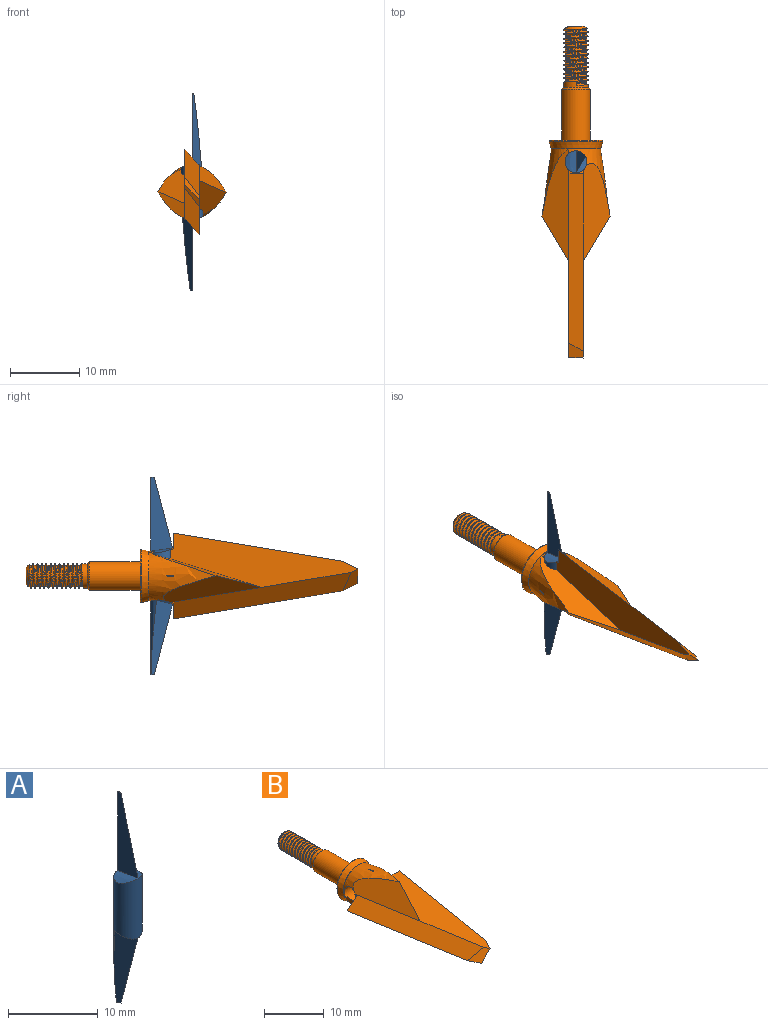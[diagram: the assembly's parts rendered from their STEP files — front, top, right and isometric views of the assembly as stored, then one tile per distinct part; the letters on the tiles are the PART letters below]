
ASSEMBLY  parts=2 mates=1
PART A: 11 faces, bbox 3.4x3.2x28.6 mm
  f0: cylinder r=1.59mm len=28.58mm, axis (0,0,-1), area 93.6mm2, adj f1,f2,f3,f4,f5,f6,f7,f8
  f1: plane 0.51x0.27mm, normal (0,0,-1), area 0.1mm2, adj f0,f3,f9
  f2: plane 0.51x0.27mm, normal (0,0,1), area 0.1mm2, adj f0,f4,f7
  f3: plane 10.69x3.18mm, normal (1,0,0), area 19.6mm2, adj f0,f1,f6,f9
  f4: plane 10.69x3.18mm, normal (-1,0,0), area 19.6mm2, adj f0,f2,f5,f7
  f5: cone r=3.56mm half-angle=8deg, axis (0,-1,0), area 4.1mm2, adj f0,f4
  f6: cone r=3.56mm half-angle=8deg, axis (0,-1,0), area 4.1mm2, adj f0,f3
  f7: plane 10.85x3.15mm, normal (0.87,-0.48,0.13), area 18.9mm2, adj f0,f2,f4,f8
  f8: cone r=3.56mm half-angle=8deg, axis (0,-1,0), area 1.6mm2, adj f0,f7
  f9: plane 10.85x3.15mm, normal (-0.87,-0.48,-0.13), area 18.9mm2, adj f0,f1,f3,f10
  f10: cone r=3.56mm half-angle=8deg, axis (0,-1,0), area 1.6mm2, adj f0,f9
PART B: 55 faces, bbox 12.4x285.9x9.8 mm
  f0: cylinder r=2.08mm len=7.37mm, axis (0,-1,0), area 96.4mm2, adj f2,f20
  f1: plane 3.66x3.66mm, normal (0,1,0), area 0.9mm2, adj f2,f36
  f2: cone r=1.83mm half-angle=45deg, axis (0,-1,0), area 4.4mm2, adj f0,f1
  f3: plane 0.63x0.29mm, normal (0,0,-1), area 0.1mm2, adj f6,f7,f30
  f4: cone r=3.56mm half-angle=8deg, axis (0,-1,0), area 37.2mm2, adj f5,f7,f18,f27,f28,f29,f30,f31
  f5: plane 0.63x0.29mm, normal (0,0,1), area 0.1mm2, adj f4,f7,f25
  f6: cone r=3.56mm half-angle=8deg, axis (0,-1,0), area 37.2mm2, adj f3,f7,f18,f22,f23,f24,f25,f26
  f7: cylinder r=1.59mm len=8.08mm, axis (-1,0,0), area 68.5mm2, adj f3,f4,f5,f6,f9,f10,f12,f13
  f8: plane 0.22x0.18mm, normal (0,-1,0), area 0mm2, adj f12,f15,f34
  f9: plane 27.15x7.85mm, normal (0,0,-1), area 108.7mm2, adj f7,f13,f17,f30,f32,f33,f34,f35
  f10: plane 27.15x7.85mm, normal (0,0,1), area 108.7mm2, adj f7,f15,f16,f25,f32,f33,f34,f35
  f11: plane 0.22x0.18mm, normal (0,-1,0), area 0mm2, adj f13,f14,f35
  f12: plane 0.48x0.18mm, normal (0,0,-1), area 0mm2, adj f7,f8,f15,f29
  f13: cone r=3.56mm half-angle=8deg, axis (0,-1,0), area 0.5mm2, adj f7,f9,f11,f14,f17
  f14: plane 0.48x0.18mm, normal (0,0,1), area 0mm2, adj f7,f11,f13,f22
  f15: cone r=3.56mm half-angle=8deg, axis (0,-1,0), area 0.5mm2, adj f7,f8,f10,f12,f16
  f16: plane 2.28x1.85mm, normal (0,1,0), area 2mm2, adj f10,f15,f34
  f17: plane 2.28x1.85mm, normal (0,1,0), area 2mm2, adj f9,f13,f35
  f18: plane 7.15x7.15mm, normal (0,-1,0), area 0.4mm2, adj f4,f6,f19
  f19: cone r=3.94mm half-angle=16deg, axis (0,1,0), area 27mm2, adj f18,f21
  f20: plane 7.54x7.54mm, normal (0,1,0), area 31mm2, adj f0,f21
  f21: torus R=3.77mm, axis (0,1,0), area 5.7mm2, adj f19,f20
  f22: plane 14.19x3.9mm, normal (-0.81,-0.13,0.57), area 44.6mm2, adj f6,f7,f14,f25,f35
  f23: bspline ~259.18x0.39mm, area 0.1mm2, adj f6,f24,f26
  f24: bspline ~259.18x0.38mm, area 0.1mm2, adj f6,f23,f26
  f25: plane 16.26x5.05mm, normal (0.95,-0.3,0.09), area 39.5mm2, adj f5,f6,f7,f10,f22
  f26: plane 0.17x0.15mm, normal (0,1,0), area 0mm2, adj f6,f23,f24
  f27: bspline ~259.18x0.39mm, area 0.1mm2, adj f4,f28,f31
  f28: bspline ~259.18x0.38mm, area 0.1mm2, adj f4,f27,f31
  f29: plane 14.19x3.9mm, normal (0.81,-0.13,-0.57), area 44.6mm2, adj f4,f7,f12,f30,f34
  f30: plane 16.26x5.05mm, normal (-0.95,-0.3,-0.09), area 39.5mm2, adj f3,f4,f7,f9,f29
  f31: plane 0.17x0.15mm, normal (0,1,0), area 0mm2, adj f4,f27,f28
  f32: plane 3.16x2.18mm, normal (-0.66,-0.34,0.66), area 4.8mm2, adj f9,f10,f33,f35
  f33: plane 3.16x2.18mm, normal (0.66,-0.34,-0.66), area 4.8mm2, adj f9,f10,f32,f34
  f34: plane 25.7x6.72mm, normal (0.63,-0.11,-0.77), area 80.4mm2, adj f8,f9,f10,f16,f29,f33
  f35: plane 25.7x6.72mm, normal (-0.63,-0.11,0.77), area 80.4mm2, adj f9,f10,f11,f17,f22,f32
  f36: cylinder r=1.75mm len=3.51mm, axis (0,-1,0), area 7.4mm2, adj f1,f37,f51,f52,f54
  f37: cylinder r=1.75mm len=3.51mm, axis (0,-1,0), area 1mm2, adj f36,f38,f52,f54
  f38: cylinder r=1.75mm len=3.51mm, axis (0,-1,0), area 1mm2, adj f37,f39,f52,f54
  f39: cylinder r=1.75mm len=3.51mm, axis (0,-1,0), area 1mm2, adj f38,f40,f52,f54
  f40: cylinder r=1.75mm len=3.51mm, axis (0,-1,0), area 1mm2, adj f39,f41,f52,f54
  f41: cylinder r=1.75mm len=3.51mm, axis (0,-1,0), area 1mm2, adj f40,f42,f52,f54
  f42: cylinder r=1.75mm len=3.51mm, axis (0,-1,0), area 1mm2, adj f41,f43,f52,f54
  f43: cylinder r=1.75mm len=3.51mm, axis (0,-1,0), area 1mm2, adj f42,f44,f52,f54
  f44: cylinder r=1.75mm len=3.51mm, axis (0,-1,0), area 1mm2, adj f43,f45,f52,f54
  f45: cylinder r=1.75mm len=3.51mm, axis (0,-1,0), area 1mm2, adj f44,f46,f52,f54
  f46: cylinder r=1.75mm len=3.51mm, axis (0,-1,0), area 1mm2, adj f45,f47,f52,f54
  f47: cylinder r=1.75mm len=3.51mm, axis (0,-1,0), area 1mm2, adj f46,f48,f52,f54
  f48: cylinder r=1.75mm len=1.33mm, axis (0,-1,0), area 0.1mm2, adj f47,f50,f54
  f49: plane 2.49x2.49mm, normal (0,1,0), area 4.9mm2, adj f50
  f50: cone r=1.24mm half-angle=45deg, axis (0,-1,0), area 4.6mm2, adj f48,f49,f52,f53,f54
  f51: plane 0.55x0.27mm, normal (0,0,-1), area 0.1mm2, adj f36,f52,f53,f54
  f52: bspline ~8.47x4.05mm, area 45.1mm2, adj f36,f37,f38,f39,f40,f41,f42,f43
  f53: cylinder r=1.48mm len=8.16mm, axis (0,1,0), area 20.7mm2, adj f50,f51,f52,f54
  f54: bspline ~8.23x4.05mm, area 41.3mm2, adj f36,f37,f38,f39,f40,f41,f42,f43
PLACE A t=(1.67,-0.58,6.24)mm
PLACE B rot(axis=(0,-1,0),90deg) t=(1.67,-4.13,6.24)mm fixed
MATE cylindrical B.f7 <-> A.f0  axis (0,0,-1) through (1.67,-2.43,6.24)mm
